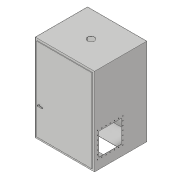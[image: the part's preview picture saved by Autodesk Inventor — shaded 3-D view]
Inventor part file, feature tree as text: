
AUTODESK INVENTOR PART (.ipt)
format: ipt  version: 2017 (Build 210142000, 142)  size: 251,904 bytes
history: native  units: in
note: dims shown in document units (in); Inventor stores cm internally (conversion verified against a paired STEP export)
features: extrude x4, sketch x4, thicken_offset x3, other x1, shell x1
ambient origin geometry x8: Origin, YZ Plane, XZ Plane, XY Plane, X Axis, Y Axis, Z Axis, Center Point
bodies: Solid1 (feature_tree)
feature tree (13):
  other  "enclosure"
  extrude  "panels"  Depth=12.9921in
  extrude  "chimney"  Depth=6.0in
  extrude  "Extrusion3"  Depth=0.3937in
  extrude  "Extrusion4"  Depth=13.7795in
  thicken_offset  "Thicken1"
  thicken_offset  "Thicken2"
  thicken_offset  "Thicken3"
  shell  "Shell1"  Thickness=1.9685in
  sketch  "Sketch1"  dims[d0=12.9921in d1=12.9921in]
  sketch  "Sketch2"  dims[d2=2.5in d3=6.0in]
  sketch  "Sketch3"  dims[d4=0.3937in d5=0.0in d6=4.0in]
  sketch  "Sketch4"  dims[d7=3.937in d8=0.0in d9=13.7795in d10=1.9685in d11=7.874in d12=1.0in d13=0.0in d14=0.75in d15=0.4724in d16=0.4724in d17=0.4724in d18=0.4724in d19=2.3622in d21=2.4154in d22=0.3937in d24=1.0in d26=2.3622in d28=2.4154in d29=0.3937in d31=1.0in d33=2.3622in d35=2.4154in d36=0.3937in d38=1.0in d40=2.3622in d42=2.4154in d43=0.3937in d45=1.0in d47=1.0in d48=0.0in d49=1.063in d50=1.063in d51=1.063in d52=1.063in d53=1.063in d54=1.063in d55=0.1181in]
